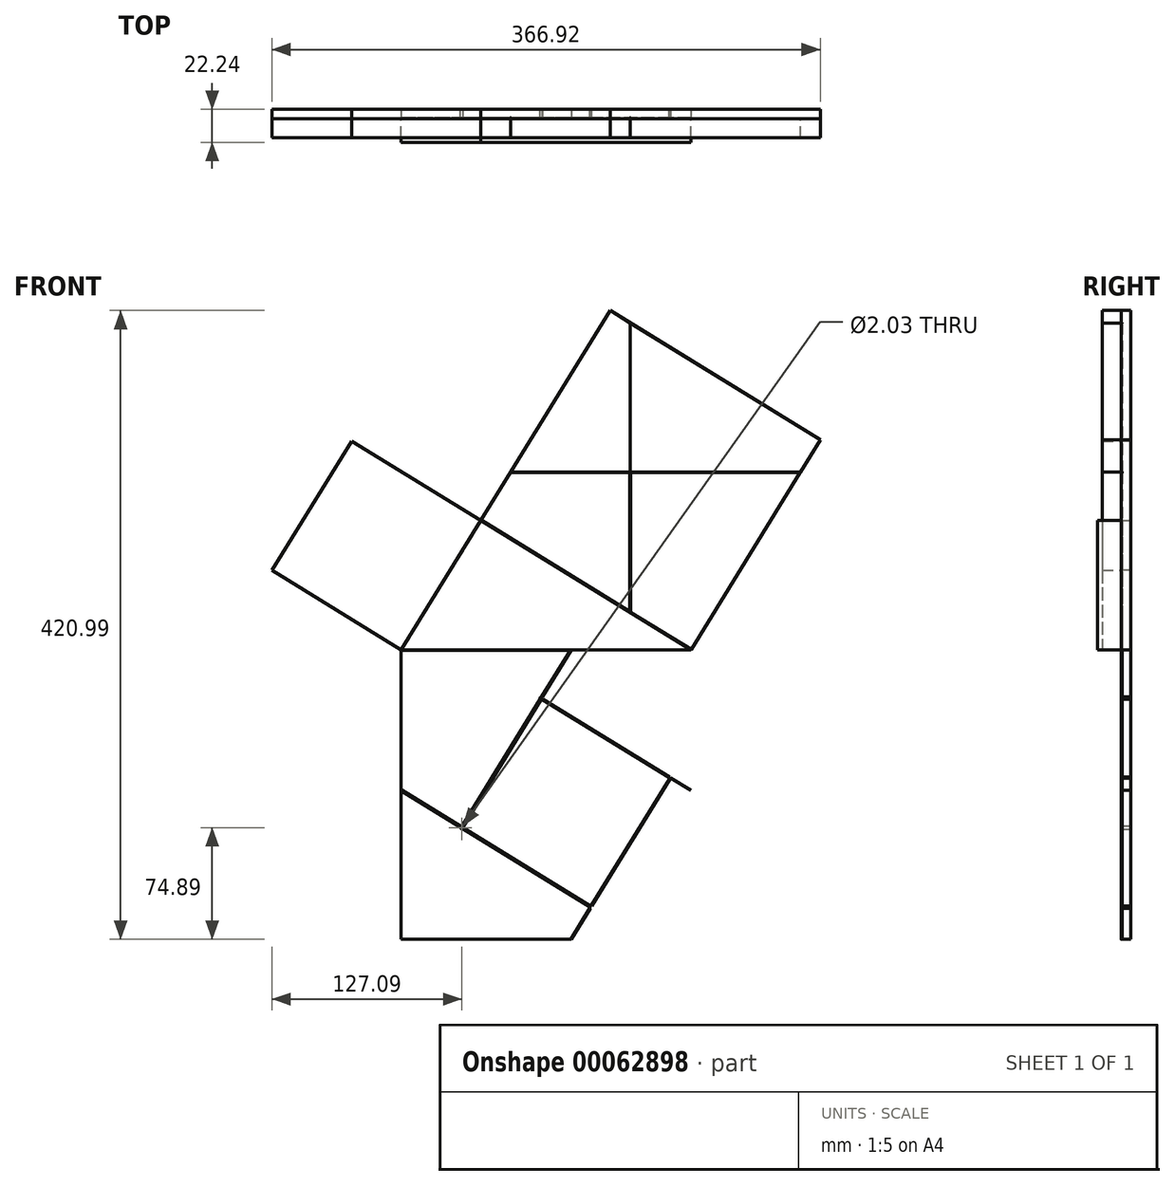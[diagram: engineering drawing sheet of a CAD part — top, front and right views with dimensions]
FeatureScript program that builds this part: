
annotation { "Feature Type Name" : "Feature", "Feature Type Description" : "" }
export const myFeature = defineFeature(function(context is Context, id is Id, definition is map)
    precondition{}
    {
        {
            var Q0;
            Q0=qCreatedBy(makeId("Front.planeOp"),FACE);
            var sketch = newSketch(context, id + "F0", { "sketchPlane" : qUnion([Q0])});
            skLineSegment(sketch, "E0", {"start": v(0, 0) * mm, "end": v(-53.25, -86.53) * mm});
            skLineSegment(sketch, "E1", {"start": v(0, 0) * mm, "end": v(140.6, -86.53) * mm});
            skLineSegment(sketch, "E2", {"start": v(140.6, -86.53) * mm, "end": v(-53.25, -86.53) * mm});
            skLineSegment(sketch, "E3", {"start": v(86.53, 140.6) * mm, "end": v(227.14, 54.08) * mm});
            skLineSegment(sketch, "E4", {"start": v(227.14, 54.08) * mm, "end": v(140.6, -86.53) * mm});
            skLineSegment(sketch, "E5", {"start": v(0, 0) * mm, "end": v(-86.53, 53.25) * mm});
            skLineSegment(sketch, "E6", {"start": v(-86.53, 53.25) * mm, "end": v(-139.78, -33.28) * mm});
            skLineSegment(sketch, "E7", {"start": v(-139.78, -33.28) * mm, "end": v(-53.25, -86.53) * mm});
            skLineSegment(sketch, "E8", {"start": v(-53.25, -86.53) * mm, "end": v(-53.25, -280.39) * mm});
            skLineSegment(sketch, "E9", {"start": v(-53.25, -280.39) * mm, "end": v(140.6, -280.39) * mm});
            skLineSegment(sketch, "E10", {"start": v(140.6, -280.39) * mm, "end": v(140.6, -86.53) * mm});
            skLineSegment(sketch, "E11", {"start": v(0, 0) * mm, "end": v(86.53, 140.6) * mm});
            skLineSegment(sketch, "E12", {"start": v(100.05, 132.29) * mm, "end": v(100.05, -61.57) * mm});
            skLineSegment(sketch, "E13", {"start": v(19.97, 32.45) * mm, "end": v(213.83, 32.45) * mm});
            skLineSegment(sketch, "E14", {"start": v(60.53, -86.53) * mm, "end": v(-12.69, -205.5) * mm});
            skLineSegment(sketch, "E15", {"start": v(40.56, -118.98) * mm, "end": v(140.6, -180.55) * mm});
            skLineSegment(sketch, "E16", {"start": v(127.09, -172.22) * mm, "end": v(60.53, -280.39) * mm});
            skLineSegment(sketch, "E17", {"start": v(-53.25, -180.55) * mm, "end": v(73.84, -258.75) * mm});
            skLineSegment(sketch, "E18", {"start": v(-86.53, 53.25) * mm, "end": v(-53.25, -86.53) * mm});
            skLineSegment(sketch, "E19", {"start": v(40.56, -118.98) * mm, "end": v(73.84, -258.75) * mm, "construction": true});
            skLineSegment(sketch, "E20", {"start": v(-12.69, -205.5) * mm, "end": v(127.09, -172.22) * mm, "construction": true});
            skLineSegment(sketch, "E21", {"start": v(19.97, 32.45) * mm, "end": v(0, 0) * mm});
            skLineSegment(sketch, "E22", {"start": v(40.56, -118.98) * mm, "end": v(60.53, -86.53) * mm});
            skLineSegment(sketch, "E23", {"start": v(86.53, 140.6) * mm, "end": v(100.05, 132.29) * mm});
            skLineSegment(sketch, "E24", {"start": v(127.09, -172.22) * mm, "end": v(140.6, -180.55) * mm});
            skSolve(sketch);
        }
        {
            var Q0;
            {var subQ0=sQuery(id+"F0.wireOp",EDGE,"E0");Q0=makeQuery(id+"F0.imprint","IMPRINT",FACE,{"disambiguationData":[TD([[makeQuery(id+"F0.imprint","IMPRINT",EDGE,{"derivedFrom":subQ0}),1.0]])]});}
            var Q1;
            Q1=makeQuery(id+"F0.imprint","IMPRINT",FACE,{"disambiguationData":[TD([[makeQuery(id+"F0.imprint","IMPRINT",EDGE,{"derivedFrom":sQuery(id+"F0.wireOp",EDGE,"E1")}),1.0]])]});
            var Q2;
            Q2=makeQuery(id+"F0.imprint","IMPRINT",FACE,{"disambiguationData":[TD([[makeQuery(id+"F0.imprint","IMPRINT",EDGE,{"derivedFrom":sQuery(id+"F0.wireOp",EDGE,"E0")}),-1.0]])]});
            var Q3;
            {var subQ1=sQuery(id+"F0.wireOp",EDGE,"E8");Q3=makeQuery(id+"F0.imprint","IMPRINT",FACE,{"disambiguationData":[TD([[makeQuery(id+"F0.imprint","IMPRINT",EDGE,{"derivedFrom":subQ1}),1.0]])]});}
            var Q4;
            {var subQ0=sQuery(id+"F0.wireOp",EDGE,"E11");Q4=makeQuery(id+"F0.imprint","IMPRINT",FACE,{"disambiguationData":[TD([[makeQuery(id+"F0.imprint","IMPRINT",EDGE,{"derivedFrom":subQ0}),-1.0]])]});}
            var Q5;
            {var subQ0=sQuery(id+"F0.wireOp",EDGE,"E3");Q5=makeQuery(id+"F0.imprint","IMPRINT",FACE,{"disambiguationData":[TD([[makeQuery(id+"F0.imprint","IMPRINT",EDGE,{"derivedFrom":subQ0}),-1.0]])]});}
            var Q6;
            Q6=makeQuery(id+"F0.imprint","IMPRINT",FACE,{"disambiguationData":[TD([[makeQuery(id+"F0.imprint","IMPRINT",EDGE,{"derivedFrom":sQuery(id+"F0.wireOp",EDGE,"E6")}),1.0]])]});
            var Q7;
            Q7=makeQuery(id+"F0.imprint","IMPRINT",FACE,{"disambiguationData":[TD([[makeQuery(id+"F0.imprint","IMPRINT",EDGE,{"derivedFrom":sQuery(id+"F0.wireOp",EDGE,"E15")}),1.0]])]});
            var Q8;
            {var subQ0=sQuery(id+"F0.wireOp",EDGE,"E14");Q8=makeQuery(id+"F0.imprint","IMPRINT",FACE,{"disambiguationData":[TD([[makeQuery(id+"F0.imprint","IMPRINT",EDGE,{"derivedFrom":subQ0}),1.0]])]});}
            var Q9;
            {var subQ6=sQuery(id+"F0.wireOp",EDGE,"E24");Q9=makeQuery(id+"F0.imprint","IMPRINT",FACE,{"disambiguationData":[TD([[makeQuery(id+"F0.imprint","IMPRINT",EDGE,{"derivedFrom":subQ6}),-1.0]])]});}
            extrude(context, id + "F1", {"entities" : qUnion([Q0, Q1, Q2, Q3, Q4, Q5, Q6, Q7, Q8, Q9]), "oppositeDirection" : true, "depth" : 6.35 * mm});
        }
        {
            var Q0;
            {var subQ5=sQuery(id+"F0.wireOp",EDGE,"E0");Q0=makeQuery(id+"F0.imprint","IMPRINT",FACE,{"disambiguationData":[TD([[makeQuery(id+"F0.imprint","IMPRINT",EDGE,{"derivedFrom":subQ5}),1.0]])]});}
            extrude(context, id + "F2", {"entities" : qUnion([Q0]), "depth" : 15.88 * mm});
        }
        {
            var Q0;
            {var subQ0=sQuery(id+"F0.wireOp",EDGE,"E3");Q0=makeQuery(id+"F0.imprint","IMPRINT",FACE,{"disambiguationData":[TD([[makeQuery(id+"F0.imprint","IMPRINT",EDGE,{"derivedFrom":subQ0}),-1.0]])]});}
            extrude(context, id + "F3", {"entities" : qUnion([Q0]), "depth" : 12.7 * mm});
        }
        {
            var Q0;
            {var subQ0=sQuery(id+"F0.wireOp",EDGE,"E11");Q0=makeQuery(id+"F0.imprint","IMPRINT",FACE,{"disambiguationData":[TD([[makeQuery(id+"F0.imprint","IMPRINT",EDGE,{"derivedFrom":subQ0}),-1.0]])]});}
            extrude(context, id + "F4", {"entities" : qUnion([Q0]), "depth" : 12.7 * mm});
        }
        {
            var Q0;
            {var subQ1=sQuery(id+"F0.wireOp",EDGE,"E1");var subQ3=sQuery(id+"F0.wireOp",EDGE,"E12");var subQ4=makeQuery(id+"F0.imprint","INTERSECT",VERTEX,{"derivedFrom":[subQ1,subQ3]});Q0=makeQuery(id+"F0.imprint","IMPRINT",FACE,{"disambiguationData":[TD([[makeQuery(id+"F0.imprint","IMPRINT",EDGE,{"disambiguationData":[TD([[subQ4,1.0]])],"derivedFrom":subQ3}),1.0]])]});}
            extrude(context, id + "F5", {"entities" : qUnion([Q0]), "depth" : 12.7 * mm});
        }
        {
            var Q0;
            {var subQ0=sQuery(id+"F0.wireOp",EDGE,"E21");Q0=makeQuery(id+"F0.imprint","IMPRINT",FACE,{"disambiguationData":[TD([[makeQuery(id+"F0.imprint","IMPRINT",EDGE,{"derivedFrom":subQ0}),1.0]])]});}
            extrude(context, id + "F6", {"entities" : qUnion([Q0]), "depth" : 12.7 * mm});
        }
        {
            var Q0;
            Q0=makeQuery(id+"F0.imprint","IMPRINT",FACE,{"disambiguationData":[TD([[makeQuery(id+"F0.imprint","IMPRINT",EDGE,{"derivedFrom":sQuery(id+"F0.wireOp",EDGE,"E0")}),-1.0]])]});
            var Q1;
            Q1=makeQuery(id+"F0.imprint","IMPRINT",FACE,{"disambiguationData":[TD([[makeQuery(id+"F0.imprint","IMPRINT",EDGE,{"derivedFrom":sQuery(id+"F0.wireOp",EDGE,"E6")}),1.0]])]});
            extrude(context, id + "F7", {"entities" : qUnion([Q0, Q1]), "depth" : 12.7 * mm});
        }
        {
            var Q0;
            {var subQ0=sQuery(id+"F0.wireOp",EDGE,"E0");Q0=makeQuery(id+"F0.imprint","IMPRINT",FACE,{"disambiguationData":[TD([[makeQuery(id+"F0.imprint","IMPRINT",EDGE,{"derivedFrom":subQ0}),1.0]])]});}
            var sketch = newSketch(context, id + "F8", { "sketchPlane" : qUnion([Q0])});
            skLineSegment(sketch, "E25.JFB.JFB", {"start": v(0, 0) * mm, "end": v(-53.25, -86.53) * mm, "construction": true});
            skLineSegment(sketch, "E25.JFF.JFF", {"start": v(0, 0) * mm, "end": v(140.6, -86.53) * mm, "construction": true});
            skLineSegment(sketch, "E25.JFJ.JFJ", {"start": v(140.6, -86.53) * mm, "end": v(-53.25, -86.53) * mm, "construction": true});
            skLineSegment(sketch, "E25.JFx.JFx", {"start": v(100.05, 132.29) * mm, "end": v(100.05, -61.57) * mm, "construction": true});
            skLineSegment(sketch, "E25.JF1.JF1", {"start": v(19.97, 32.45) * mm, "end": v(213.83, 32.45) * mm, "construction": true});
            skLineSegment(sketch, "E25.JF5.JF5", {"start": v(60.53, -86.53) * mm, "end": v(-12.69, -205.5) * mm, "construction": true});
            skLineSegment(sketch, "E25.JF9.JF9", {"start": v(40.56, -118.98) * mm, "end": v(140.6, -180.55) * mm, "construction": true});
            skLineSegment(sketch, "E25.KFBB.KFBB", {"start": v(127.09, -172.22) * mm, "end": v(60.53, -280.39) * mm, "construction": true});
            skLineSegment(sketch, "E25.KFFB.KFFB", {"start": v(-53.25, -180.55) * mm, "end": v(73.84, -258.75) * mm, "construction": true});
            skArc(sketch, "E25.0.startCap", {"start": v(-0.32, 0.2) * mm, "mid": v(0.2, 0.32) * mm, "end": v(0.32, -0.2) * mm});
            skArc(sketch, "E25.0.endCap", {"start": v(-52.92, -86.73) * mm, "mid": v(-53.45, -86.85) * mm, "end": v(-53.57, -86.33) * mm});
            skLineSegment(sketch, "E25.0.left", {"start": v(0.32, -0.2) * mm, "end": v(-52.92, -86.73) * mm});
            skLineSegment(sketch, "E25.0.right", {"start": v(-0.32, 0.2) * mm, "end": v(-53.57, -86.33) * mm});
            skArc(sketch, "E25.1.startCap", {"start": v(-0.2, -0.32) * mm, "mid": v(-0.32, 0.2) * mm, "end": v(0.2, 0.32) * mm});
            skArc(sketch, "E25.1.endCap", {"start": v(140.8, -86.2) * mm, "mid": v(140.93, -86.73) * mm, "end": v(140.4, -86.85) * mm});
            skLineSegment(sketch, "E25.1.left", {"start": v(0.2, 0.32) * mm, "end": v(140.8, -86.2) * mm});
            skLineSegment(sketch, "E25.1.right", {"start": v(-0.2, -0.32) * mm, "end": v(140.4, -86.85) * mm});
            skArc(sketch, "E25.2.startCap", {"start": v(140.6, -86.15) * mm, "mid": v(140.99, -86.53) * mm, "end": v(140.6, -86.9) * mm});
            skArc(sketch, "E25.2.endCap", {"start": v(-53.25, -86.9) * mm, "mid": v(-53.63, -86.53) * mm, "end": v(-53.25, -86.15) * mm});
            skLineSegment(sketch, "E25.2.left", {"start": v(140.6, -86.9) * mm, "end": v(-53.25, -86.9) * mm});
            skLineSegment(sketch, "E25.2.right", {"start": v(140.6, -86.15) * mm, "end": v(-53.25, -86.15) * mm});
            skArc(sketch, "E25.3.startCap", {"start": v(99.67, 132.29) * mm, "mid": v(100.05, 132.67) * mm, "end": v(100.43, 132.29) * mm});
            skArc(sketch, "E25.3.endCap", {"start": v(100.43, -61.57) * mm, "mid": v(100.05, -61.95) * mm, "end": v(99.67, -61.57) * mm});
            skLineSegment(sketch, "E25.3.left", {"start": v(100.43, 132.29) * mm, "end": v(100.43, -61.57) * mm});
            skLineSegment(sketch, "E25.3.right", {"start": v(99.67, 132.29) * mm, "end": v(99.67, -61.57) * mm});
            skArc(sketch, "E25.4.startCap", {"start": v(19.97, 32.07) * mm, "mid": v(19.59, 32.45) * mm, "end": v(19.97, 32.83) * mm});
            skArc(sketch, "E25.4.endCap", {"start": v(213.83, 32.83) * mm, "mid": v(214.2, 32.45) * mm, "end": v(213.83, 32.07) * mm});
            skLineSegment(sketch, "E25.4.left", {"start": v(19.97, 32.83) * mm, "end": v(213.83, 32.83) * mm});
            skLineSegment(sketch, "E25.4.right", {"start": v(19.97, 32.07) * mm, "end": v(213.83, 32.07) * mm});
            skArc(sketch, "E25.5.startCap", {"start": v(60.2, -86.33) * mm, "mid": v(60.73, -86.2) * mm, "end": v(60.85, -86.73) * mm});
            skArc(sketch, "E25.5.endCap", {"start": v(-12.36, -205.7) * mm, "mid": v(-12.89, -205.83) * mm, "end": v(-13.01, -205.3) * mm});
            skLineSegment(sketch, "E25.5.left", {"start": v(60.85, -86.73) * mm, "end": v(-12.36, -205.7) * mm});
            skLineSegment(sketch, "E25.5.right", {"start": v(60.2, -86.33) * mm, "end": v(-13.01, -205.3) * mm});
            skArc(sketch, "E25.6.startCap", {"start": v(40.36, -119.3) * mm, "mid": v(40.24, -118.78) * mm, "end": v(40.76, -118.65) * mm});
            skArc(sketch, "E25.6.endCap", {"start": v(140.8, -180.22) * mm, "mid": v(140.93, -180.74) * mm, "end": v(140.4, -180.87) * mm});
            skLineSegment(sketch, "E25.6.left", {"start": v(40.76, -118.65) * mm, "end": v(140.8, -180.22) * mm});
            skLineSegment(sketch, "E25.6.right", {"start": v(40.36, -119.3) * mm, "end": v(140.4, -180.87) * mm});
            skArc(sketch, "E25.7.startCap", {"start": v(126.76, -172.03) * mm, "mid": v(127.29, -171.9) * mm, "end": v(127.41, -172.42) * mm});
            skArc(sketch, "E25.7.endCap", {"start": v(60.85, -280.59) * mm, "mid": v(60.33, -280.71) * mm, "end": v(60.2, -280.19) * mm});
            skLineSegment(sketch, "E25.7.left", {"start": v(127.41, -172.42) * mm, "end": v(60.85, -280.59) * mm});
            skLineSegment(sketch, "E25.7.right", {"start": v(126.76, -172.03) * mm, "end": v(60.2, -280.19) * mm});
            skArc(sketch, "E25.8.startCap", {"start": v(-53.45, -180.87) * mm, "mid": v(-53.57, -180.35) * mm, "end": v(-53.05, -180.22) * mm});
            skArc(sketch, "E25.8.endCap", {"start": v(74.04, -258.43) * mm, "mid": v(74.16, -258.95) * mm, "end": v(73.64, -259.08) * mm});
            skLineSegment(sketch, "E25.8.left", {"start": v(-53.05, -180.22) * mm, "end": v(74.04, -258.43) * mm});
            skLineSegment(sketch, "E25.8.right", {"start": v(-53.45, -180.87) * mm, "end": v(73.64, -259.08) * mm});
            skSolve(sketch);
        }
        {
            var Q0;
            Q0 = qSketchRegion(id + "F8", true);
            extrude(context, id + "F9", {"entities" : qUnion([Q0]), "operationType" : NewBodyOperationType.REMOVE, "oppositeDirection" : true, "depth" : 0.76 * mm});
        }
        {
            var Q0;
            Q0=sQuery(id+"F0.wireOp",VERTEX,"E19.start");
            var Q1;
            Q1=sQuery(id+"F0.wireOp",VERTEX,"E20.end");
            var Q2;
            Q2=sQuery(id+"F0.wireOp",VERTEX,"E19.end");
            var Q3;
            Q3=sQuery(id+"F0.wireOp",VERTEX,"E14.end");
            var Q4;
            Q4=makeQuery(id+"F1.opExtrude","SWEPT_BODY",BODY,{"disambiguationData":[OSD([sQuery(id+"F0.wireOp",EDGE,"E3"),sQuery(id+"F0.wireOp",EDGE,"E4"),sQuery(id+"F0.wireOp",EDGE,"E5"),sQuery(id+"F0.wireOp",EDGE,"E6"),sQuery(id+"F0.wireOp",EDGE,"E7"),sQuery(id+"F0.wireOp",EDGE,"E8"),sQuery(id+"F0.wireOp",EDGE,"E9"),sQuery(id+"F0.wireOp",EDGE,"E10"),sQuery(id+"F0.wireOp",EDGE,"E11"),sQuery(id+"F0.wireOp",EDGE,"E21"),sQuery(id+"F0.wireOp",EDGE,"E23")])]});
            hole(context, id + "F10", {"style" : HoleStyle.SIMPLE, "holeDiameter" : 2.03 * mm, "endStyle" : HoleEndStyle.THROUGH, "locations" : qUnion([Q0, Q1, Q2, Q3]), "scope" : qUnion([Q4])});
        }
    });
